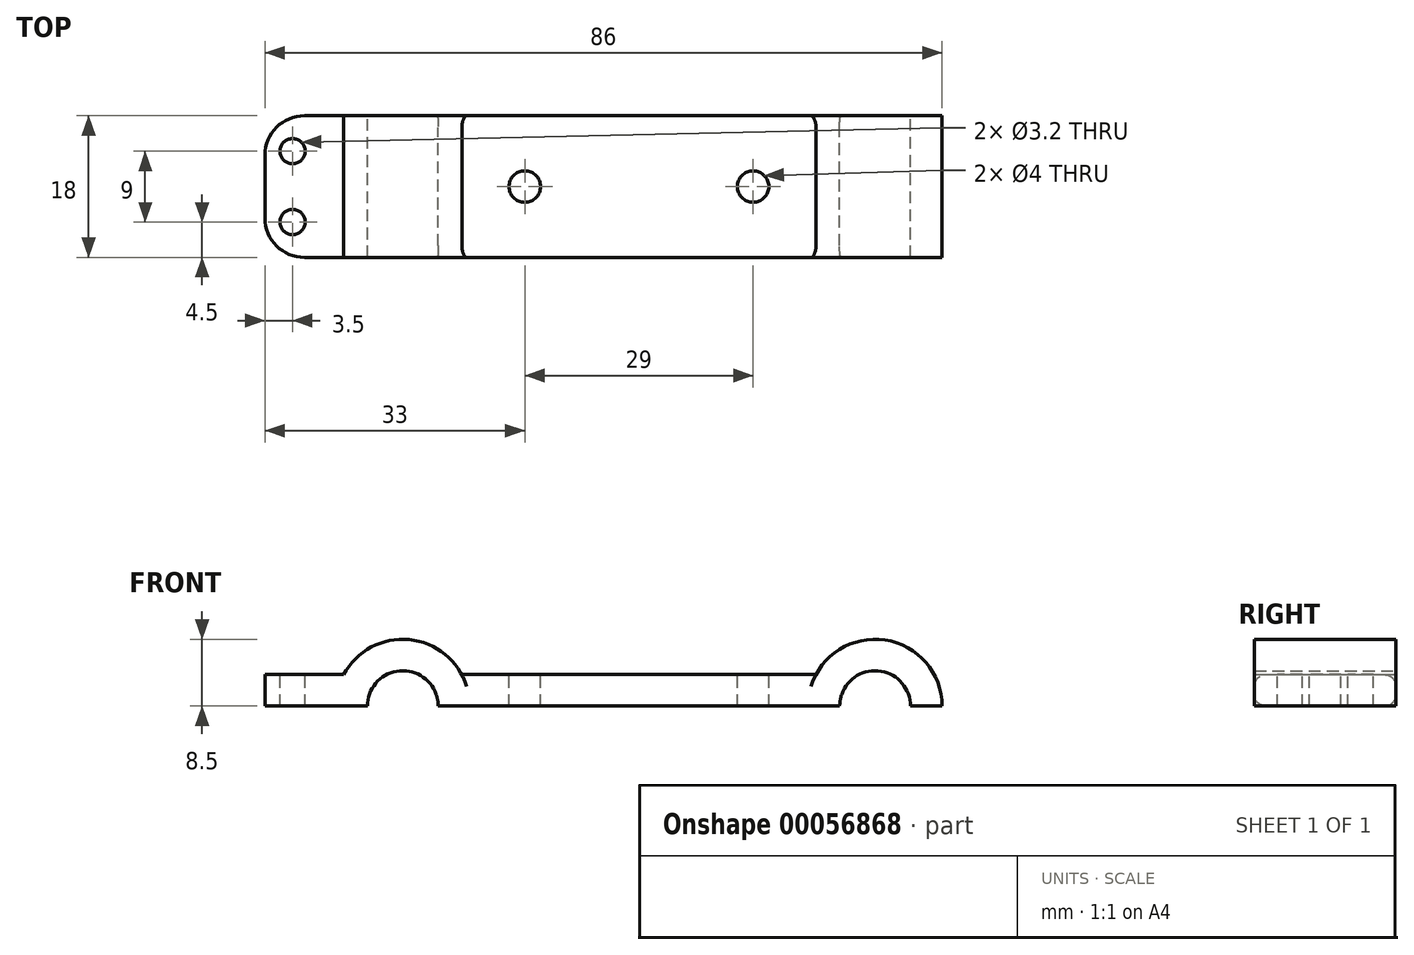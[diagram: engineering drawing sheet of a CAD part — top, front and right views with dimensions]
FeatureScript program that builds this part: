
annotation { "Feature Type Name" : "Feature", "Feature Type Description" : "" }
export const myFeature = defineFeature(function(context is Context, id is Id, definition is map)
    precondition{}
    {
        {
            var Q0;
            Q0=qCreatedBy(makeId("Front.planeOp"),FACE);
            var sketch = newSketch(context, id + "F0", { "sketchPlane" : qUnion([Q0])});
            skLineSegment(sketch, "E0", {"start": v(47.36, 0) * mm, "end": v(-25.5, 0) * mm, "construction": true});
            skLineSegment(sketch, "E1", {"start": v(0, 20.06) * mm, "end": v(0, -9.96) * mm, "construction": true});
            skLineSegment(sketch, "E2.0", {"start": v(-30, 20.06) * mm, "end": v(-30, -9.96) * mm, "construction": true});
            skLineSegment(sketch, "E3.0", {"start": v(30, 20.06) * mm, "end": v(30, -9.96) * mm, "construction": true});
            skCircle(sketch, "E4", {"center": v(30, 0) * mm, "radius": 4.5 * mm});
            skCircle(sketch, "E5", {"center": v(-30, 0) * mm, "radius": 4.5 * mm});
            skLineSegment(sketch, "E6.0", {"start": v(-38.5, 20.06) * mm, "end": v(-38.5, -9.96) * mm, "construction": true});
            skLineSegment(sketch, "E7.0", {"start": v(38.5, 20.06) * mm, "end": v(38.5, -9.96) * mm, "construction": true});
            skArc(sketch, "E8", {"start": v(-22.5, 4) * mm, "mid": v(-30, 8.5) * mm, "end": v(-37.5, 4) * mm});
            skArc(sketch, "E9", {"start": v(38.5, 0) * mm, "mid": v(32.06, 8.25) * mm, "end": v(22.5, 4) * mm});
            skLineSegment(sketch, "E10.0", {"start": v(-47.5, 20.06) * mm, "end": v(-47.5, -9.96) * mm});
            skLineSegment(sketch, "E11", {"start": v(-34.5, 0) * mm, "end": v(-47.5, 0) * mm});
            skLineSegment(sketch, "E12.0", {"start": v(-34.5, 4) * mm, "end": v(-44.5, 4) * mm});
            skLineSegment(sketch, "E13.trimOffspring", {"start": v(-30, 0) * mm, "end": v(-62.92, 0) * mm, "construction": true});
            skLineSegment(sketch, "E14", {"start": v(-34.5, 0) * mm, "end": v(-38.5, 0) * mm});
            skLineSegment(sketch, "E15", {"start": v(-25.5, 0) * mm, "end": v(25.5, 0) * mm});
            skLineSegment(sketch, "E16.0", {"start": v(-25.5, 4) * mm, "end": v(25.5, 4) * mm});
            skLineSegment(sketch, "E17", {"start": v(34.5, 0) * mm, "end": v(38.5, 0) * mm});
            skLineSegment(sketch, "E18", {"start": v(-44.5, 4) * mm, "end": v(-47.5, 4) * mm});
            skSolve(sketch);
        }
        {
            var Q0;
            {var subQ1=sQuery(id+"F0.wireOp",EDGE,"E8");Q0=makeQuery(id+"F0.imprint","IMPRINT",FACE,{"disambiguationData":[TD([[makeQuery(id+"F0.imprint","IMPRINT",EDGE,{"derivedFrom":subQ1}),1.0]])]});}
            extrude(context, id + "F1", {"entities" : qUnion([Q0]), "depth" : 18 * mm});
        }
        {
            var Q0;
            Q0=makeQuery(id+"F1.opExtrude","CAP_EDGE",EDGE,{"disambiguationData":[OSD([sQuery(id+"F0.wireOp",EDGE,"E10.0")])],"isStart":false});
            var Q1;
            Q1=makeQuery(id+"F1.opExtrude","CAP_EDGE",EDGE,{"disambiguationData":[OSD([sQuery(id+"F0.wireOp",EDGE,"E10.0")])],"isStart":true});
            fillet(context, id + "F2", {"entities" : qUnion([Q0, Q1]), "radius" : 5 * mm, "tangentPropagation" : true, "allowEdgeOverflow" : false});
        }
        {
            var Q0;
            Q0=makeQuery(id+"F1.opExtrude","CAP_EDGE",EDGE,{"disambiguationData":[OSD([sQuery(id+"F0.wireOp",EDGE,"E16.0")])],"isStart":false});
            var Q1;
            Q1=makeQuery(id+"F1.opExtrude","CAP_EDGE",EDGE,{"disambiguationData":[OSD([sQuery(id+"F0.wireOp",EDGE,"E15")])],"isStart":false});
            var Q2;
            Q2=makeQuery(id+"F1.opExtrude","CAP_EDGE",EDGE,{"disambiguationData":[OSD([sQuery(id+"F0.wireOp",EDGE,"E16.0")])],"isStart":true});
            var Q3;
            Q3=makeQuery(id+"F1.opExtrude","CAP_EDGE",EDGE,{"disambiguationData":[OSD([sQuery(id+"F0.wireOp",EDGE,"E15")])],"isStart":true});
            fillet(context, id + "F3", {"entities" : qUnion([Q0, Q1, Q2, Q3]), "radius" : 1.5 * mm, "tangentPropagation" : true, "allowEdgeOverflow" : false});
        }
        {
            var Q0;
            Q0=makeQuery(id+"F1.opExtrude","SWEPT_FACE",FACE,{"disambiguationData":[OSD([sQuery(id+"F0.wireOp",EDGE,"E16.0")])]});
            var sketch = newSketch(context, id + "F4", { "sketchPlane" : qUnion([Q0])});
            skLineSegment(sketch, "E19.0.0", {"start": v(22.5, -16.5) * mm, "end": v(22.5, -1.5) * mm});
            skLineSegment(sketch, "E19.0.1", {"start": v(22.5, -1.5) * mm, "end": v(-22.5, -1.5) * mm});
            skLineSegment(sketch, "E19.0.2", {"start": v(-22.5, -1.5) * mm, "end": v(-22.5, -16.5) * mm});
            skLineSegment(sketch, "E19.0.3", {"start": v(-22.5, -16.5) * mm, "end": v(22.5, -16.5) * mm});
            skLineSegment(sketch, "E20.0.0", {"start": v(-37.5, 0) * mm, "end": v(-42.5, 0) * mm});
            skArc(sketch, "E20.0.1", {"start": v(-42.5, 0) * mm, "mid": v(-46.04, -1.46) * mm, "end": v(-47.5, -5) * mm});
            skLineSegment(sketch, "E20.0.2", {"start": v(-47.5, -5) * mm, "end": v(-47.5, -13) * mm});
            skArc(sketch, "E20.0.3", {"start": v(-47.5, -13) * mm, "mid": v(-46.04, -16.54) * mm, "end": v(-42.5, -18) * mm});
            skLineSegment(sketch, "E20.0.4", {"start": v(-42.5, -18) * mm, "end": v(-37.5, -18) * mm});
            skLineSegment(sketch, "E20.0.5", {"start": v(-37.5, -18) * mm, "end": v(-37.5, 0) * mm});
            skLineSegment(sketch, "E21", {"start": v(-47.5, -9) * mm, "end": v(-37.5, -9) * mm});
            skLineSegment(sketch, "E22", {"start": v(-22.5, -9) * mm, "end": v(22.5, -9) * mm, "construction": true});
            skLineSegment(sketch, "E23.0", {"start": v(-47.5, -13.5) * mm, "end": v(-40.5, -13.5) * mm, "construction": true});
            skLineSegment(sketch, "E24.0", {"start": v(-47.5, -4.5) * mm, "end": v(-40.5, -4.5) * mm, "construction": true});
            skLineSegment(sketch, "E25", {"start": v(-44, -4.5) * mm, "end": v(-44, -13.5) * mm, "construction": true});
            skCircle(sketch, "E26", {"center": v(-44, -4.5) * mm, "radius": 1.6 * mm});
            skCircle(sketch, "E27", {"center": v(-44, -13.5) * mm, "radius": 1.6 * mm});
            skLineSegment(sketch, "E28.0", {"start": v(14.5, -16.5) * mm, "end": v(14.5, -1.5) * mm, "construction": true});
            skLineSegment(sketch, "E29.0", {"start": v(-14.5, -1.5) * mm, "end": v(-14.5, -16.5) * mm, "construction": true});
            skCircle(sketch, "E30", {"center": v(-14.5, -9) * mm, "radius": 2 * mm});
            skCircle(sketch, "E31", {"center": v(14.5, -9) * mm, "radius": 2 * mm});
            skSolve(sketch);
        }
        {
            var Q0;
            Q0=makeQuery(id+"F4.imprint","IMPRINT",FACE,{"disambiguationData":[TD([[makeQuery(id+"F4.imprint","IMPRINT",EDGE,{"derivedFrom":sQuery(id+"F4.wireOp",EDGE,"E26")}),1.0]])]});
            var Q1;
            Q1=makeQuery(id+"F4.imprint","IMPRINT",FACE,{"disambiguationData":[TD([[makeQuery(id+"F4.imprint","IMPRINT",EDGE,{"derivedFrom":sQuery(id+"F4.wireOp",EDGE,"E27")}),1.0]])]});
            var Q2;
            Q2=makeQuery(id+"F1.opExtrude","SWEPT_FACE",FACE,{"disambiguationData":[OSD([sQuery(id+"F0.wireOp",EDGE,"E11"),sQuery(id+"F0.wireOp",EDGE,"E14")])]});
            extrude(context, id + "F5", {"entities" : qUnion([Q0, Q1]), "operationType" : NewBodyOperationType.REMOVE, "endBound" : BoundingType.UP_TO_SURFACE, "oppositeDirection" : true, "endBoundEntityFace" : qUnion([Q2]), "depth" : 25 * mm});
        }
        {
            var Q0;
            Q0=makeQuery(id+"F4.imprint","IMPRINT",FACE,{"disambiguationData":[TD([[makeQuery(id+"F4.imprint","IMPRINT",EDGE,{"derivedFrom":sQuery(id+"F4.wireOp",EDGE,"E31")}),1.0]])]});
            var Q1;
            Q1=makeQuery(id+"F4.imprint","IMPRINT",FACE,{"disambiguationData":[TD([[makeQuery(id+"F4.imprint","IMPRINT",EDGE,{"derivedFrom":sQuery(id+"F4.wireOp",EDGE,"E30")}),1.0]])]});
            var Q2;
            Q2=makeQuery(id+"F1.opExtrude","SWEPT_FACE",FACE,{"disambiguationData":[OSD([sQuery(id+"F0.wireOp",EDGE,"E15")])]});
            extrude(context, id + "F6", {"entities" : qUnion([Q0, Q1]), "operationType" : NewBodyOperationType.REMOVE, "endBound" : BoundingType.UP_TO_SURFACE, "oppositeDirection" : true, "endBoundEntityFace" : qUnion([Q2]), "depth" : 25 * mm});
        }
    });
